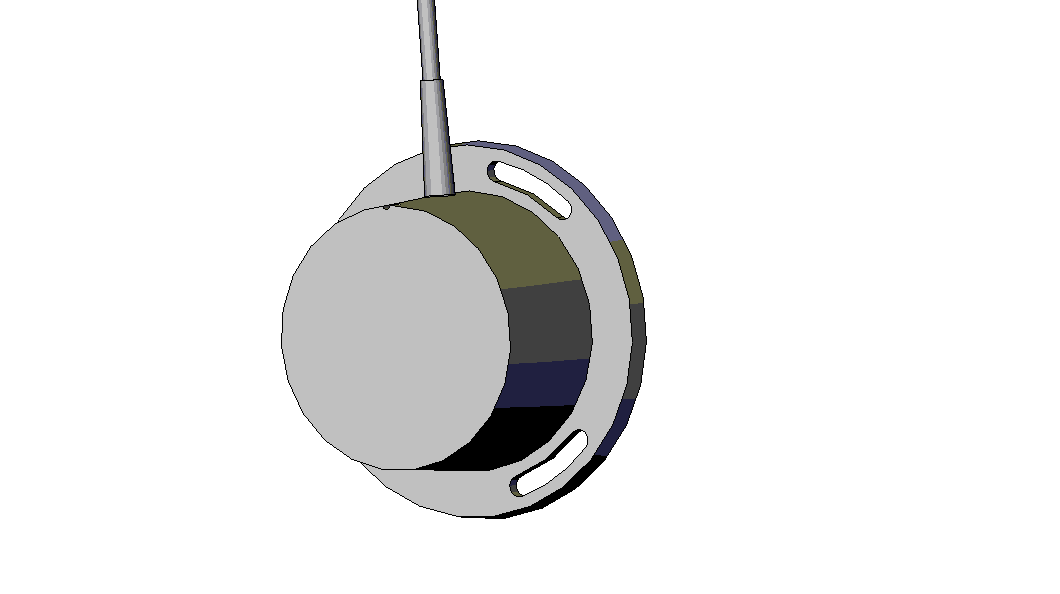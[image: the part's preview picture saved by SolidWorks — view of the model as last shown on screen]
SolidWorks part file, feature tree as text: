
SOLIDWORKS PART (.sldprt)
format: sldprt  version: not decoded by parser v0  size: 205,312 bytes
history: native  units: mm
features: sketch x6, plane x3, extrude x3, cut_extrude x2, material x1, revolve x1, pattern_circular x1 (+8 scaffold rows collapsed)
feature tree (25):
  scaffold x8  (default folders/planes/origin — collapsed)
  material  "Matériau <non spécifié>"
  plane  "Face"
  plane  "Dessus"
  plane  "Droite"
  sketch  "Esquisse1"  dims[D12=1.5mm D1=45.0mm D2=6.0mm D3=49.25mm D4=48.5mm D5=36.5mm D6=34.5mm D7=3.5mm D8=3.5mm D9=12.5mm D10=3.5mm D11=2.0mm]
  revolve  "Révolution1"  Angle=360deg
  sketch  "Esquisse2"  dims[D2=2.0mm D1=34.5mm]
  cut_extrude  "Enlèv. mat.-Extru.1"  Depth=5.5mm
  sketch  "Esquisse3"  dims[D2=8.0mm D1=17.0mm]
  extrude  "Extrusion1"  Depth=36mm
  sketch  "Esquisse4"
  extrude  "Extrusion2"  Depth=30mm
  sketch  "Esquisse5"  dims[D1=4.5mm]
  extrude  "Extrusion3"  Depth=30mm
  sketch  "Esquisse6"  dims[c1.D1=85.0mm c1.D2=5.5mm c1.D3=11.0mm c2.D1=42.5mm]
  cut_extrude  "Enlèv. mat.-Extru.2"  [1 undecoded]
  pattern_circular  "Répétition circulaire1"  Count=3 Angle=120deg
decode coverage: 11 of 13 modeling features carry decoded parameters
note: 1 parameter value undecoded
note: suppression state not decoded; provenance and decode notes live in map.json
